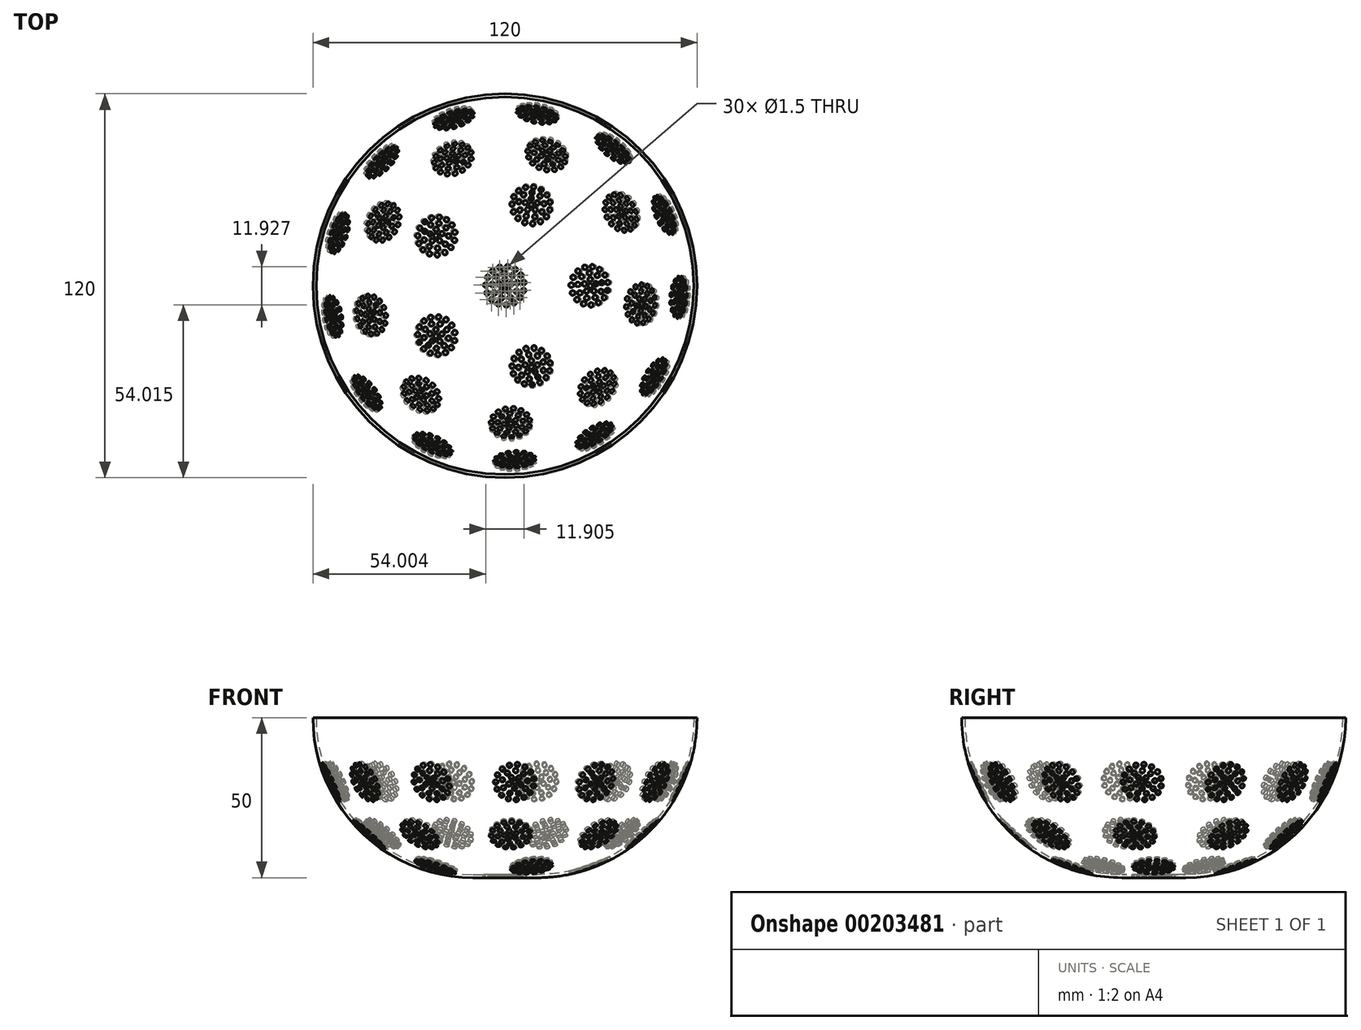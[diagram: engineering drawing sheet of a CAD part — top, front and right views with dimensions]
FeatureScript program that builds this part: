
annotation { "Feature Type Name" : "Feature", "Feature Type Description" : "" }
export const myFeature = defineFeature(function(context is Context, id is Id, definition is map)
    precondition{}
    {
        {
            var Q0;
            Q0=qCreatedBy(makeId("Front.planeOp"),FACE);
            var sketch = newSketch(context, id + "F0", { "sketchPlane" : qUnion([Q0])});
            skLineSegment(sketch, "E0", {"start": v(0, 0) * mm, "end": v(10, 0) * mm});
            skArc(sketch, "E1", {"start": v(10, 0) * mm, "mid": v(45.36, 14.64) * mm, "end": v(60, 50) * mm});
            skLineSegment(sketch, "E2", {"start": v(0, 0) * mm, "end": v(0, 50) * mm});
            skLineSegment(sketch, "E3", {"start": v(0, 50) * mm, "end": v(60, 50) * mm});
            skArc(sketch, "E4.0", {"start": v(10, 1) * mm, "mid": v(44.65, 15.35) * mm, "end": v(59, 50) * mm});
            skLineSegment(sketch, "E4.1", {"start": v(0, 1) * mm, "end": v(10, 1) * mm});
            skSolve(sketch);
        }
        {
            var Q0;
            {var subQ2=sQuery(id+"F0.wireOp",EDGE,"E0");Q0=makeQuery(id+"F0.imprint","IMPRINT",FACE,{"disambiguationData":[TD([[makeQuery(id+"F0.imprint","IMPRINT",EDGE,{"derivedFrom":subQ2}),1.0]])]});}
            var Q1;
            Q1=sQuery(id+"F0.wireOp",EDGE,"E2");
            revolve(context, id + "F1", {"entities" : qUnion([Q0]), "axis" : qUnion([Q1]), "revolveType" : RevolveType.FULL});
        }
        {
            var Q0;
            Q0=makeQuery(id+"F1.opRevolve","SWEPT_FACE",FACE,{"disambiguationData":[OSD([sQuery(id+"F0.wireOp",EDGE,"E4.1")])]});
            var sketch = newSketch(context, id + "F2", { "sketchPlane" : qUnion([Q0])});
            skCircle(sketch, "E5", {"center": v(0, 0) * mm, "radius": 0.75 * mm});
            skCircle(sketch, "E6", {"center": v(0, 2) * mm, "radius": 0.75 * mm});
            skCircle(sketch, "E7.1.0", {"center": v(-1.9, 0.62) * mm, "radius": 0.75 * mm});
            skCircle(sketch, "E7.2.0", {"center": v(-1.18, -1.62) * mm, "radius": 0.75 * mm});
            skCircle(sketch, "E7.3.0", {"center": v(1.18, -1.62) * mm, "radius": 0.75 * mm});
            skCircle(sketch, "E7.4.0", {"center": v(1.9, 0.62) * mm, "radius": 0.75 * mm});
            skLineSegment(sketch, "E8", {"start": v(0, 2) * mm, "end": v(1.9, 0.62) * mm, "construction": true});
            skLineSegment(sketch, "E9", {"start": v(0, 0) * mm, "end": v(0.95, 1.3) * mm, "construction": true});
            skLineSegment(sketch, "E10", {"start": v(0.95, 1.3) * mm, "end": v(2.35, 3.24) * mm, "construction": true});
            skCircle(sketch, "E11", {"center": v(2.35, 3.24) * mm, "radius": 0.75 * mm});
            skCircle(sketch, "E12.1.0", {"center": v(-0.28, 4) * mm, "radius": 0.75 * mm});
            skCircle(sketch, "E12.2.0", {"center": v(-2.78, 2.88) * mm, "radius": 0.75 * mm});
            skCircle(sketch, "E12.3.0", {"center": v(-3.98, 0.42) * mm, "radius": 0.75 * mm});
            skCircle(sketch, "E12.4.0", {"center": v(-3.32, -2.24) * mm, "radius": 0.75 * mm});
            skCircle(sketch, "E12.5.0", {"center": v(-1.1, -3.85) * mm, "radius": 0.75 * mm});
            skCircle(sketch, "E12.6.0", {"center": v(1.63, -3.65) * mm, "radius": 0.75 * mm});
            skCircle(sketch, "E13.1.7.0", {"center": v(3.6, -1.75) * mm, "radius": 0.75 * mm});
            skCircle(sketch, "E13.1.8.0", {"center": v(3.88, 0.97) * mm, "radius": 0.75 * mm});
            skLineSegment(sketch, "E14", {"start": v(3.88, 0.97) * mm, "end": v(2.35, 3.24) * mm, "construction": true});
            skLineSegment(sketch, "E15", {"start": v(0, 0) * mm, "end": v(3.12, 2.1) * mm, "construction": true});
            skLineSegment(sketch, "E16", {"start": v(3.12, 2.1) * mm, "end": v(4.97, 3.36) * mm, "construction": true});
            skCircle(sketch, "E17", {"center": v(4.97, 3.36) * mm, "radius": 0.75 * mm});
            skCircle(sketch, "E18.1.0", {"center": v(3.18, 5.09) * mm, "radius": 0.75 * mm});
            skCircle(sketch, "E18.2.0", {"center": v(0.84, 5.94) * mm, "radius": 0.75 * mm});
            skCircle(sketch, "E18.3.0", {"center": v(-1.65, 5.77) * mm, "radius": 0.75 * mm});
            skCircle(sketch, "E18.4.0", {"center": v(-3.86, 4.6) * mm, "radius": 0.75 * mm});
            skCircle(sketch, "E18.5.0", {"center": v(-5.4, 2.63) * mm, "radius": 0.75 * mm});
            skCircle(sketch, "E18.6.0", {"center": v(-6, 0.2) * mm, "radius": 0.75 * mm});
            skCircle(sketch, "E18.7.0", {"center": v(-5.56, -2.25) * mm, "radius": 0.75 * mm});
            skCircle(sketch, "E18.8.0", {"center": v(-4.17, -4.32) * mm, "radius": 0.75 * mm});
            skCircle(sketch, "E18.9.0", {"center": v(-2.05, -5.64) * mm, "radius": 0.75 * mm});
            skCircle(sketch, "E18.10.0", {"center": v(0.42, -5.99) * mm, "radius": 0.75 * mm});
            skCircle(sketch, "E18.11.0", {"center": v(2.82, -5.3) * mm, "radius": 0.75 * mm});
            skCircle(sketch, "E18.12.0", {"center": v(4.73, -3.7) * mm, "radius": 0.75 * mm});
            skCircle(sketch, "E18.13.0", {"center": v(5.82, -1.45) * mm, "radius": 0.75 * mm});
            skCircle(sketch, "E18.14.0", {"center": v(5.9, 1.04) * mm, "radius": 0.75 * mm});
            skSolve(sketch);
        }
        {
            var Q0;
            Q0=qSketchRegion(id+"F2",true);
            extrude(context, id + "F3", {"entities" : qUnion([Q0]), "operationType" : NewBodyOperationType.REMOVE, "oppositeDirection" : true, "depth" : 25 * mm});
        }
        {
            var Q0;
            Q0=makeQuery(id+"F1.opRevolve","SWEPT_FACE",FACE,{"disambiguationData":[OSD([sQuery(id+"F0.wireOp",EDGE,"E3")])]});
            var sketch = newSketch(context, id + "F4", { "sketchPlane" : qUnion([Q0])});
            skLineSegment(sketch, "E19", {"start": v(0, 59) * mm, "end": v(0, -59) * mm});
            skLineSegment(sketch, "E20", {"start": v(0, 0) * mm, "end": v(-31.56, 49.85) * mm});
            skLineSegment(sketch, "E21", {"start": v(0, 0) * mm, "end": v(-46.28, 36.6) * mm});
            skSolve(sketch);
        }
        {
            var Q0;
            Q0=makeQuery(id+"F3.boolean.opBoolean","COPY",FACE,{"derivedFrom":makeQuery(id+"F3.opExtrude","SWEPT_FACE",FACE,{"disambiguationData":[OSD([sQuery(id+"F2.wireOp",EDGE,"E18.7.0")])]})});
            var Q1;
            Q1=makeQuery(id+"F3.boolean.opBoolean","COPY",FACE,{"derivedFrom":makeQuery(id+"F3.opExtrude","SWEPT_FACE",FACE,{"disambiguationData":[OSD([sQuery(id+"F2.wireOp",EDGE,"E18.6.0")])]})});
            var Q2;
            Q2=makeQuery(id+"F3.boolean.opBoolean","COPY",FACE,{"derivedFrom":makeQuery(id+"F3.opExtrude","SWEPT_FACE",FACE,{"disambiguationData":[OSD([sQuery(id+"F2.wireOp",EDGE,"E18.5.0")])]})});
            var Q3;
            Q3=makeQuery(id+"F3.boolean.opBoolean","COPY",FACE,{"derivedFrom":makeQuery(id+"F3.opExtrude","SWEPT_FACE",FACE,{"disambiguationData":[OSD([sQuery(id+"F2.wireOp",EDGE,"E18.4.0")])]})});
            var Q4;
            Q4=makeQuery(id+"F3.boolean.opBoolean","COPY",FACE,{"derivedFrom":makeQuery(id+"F3.opExtrude","SWEPT_FACE",FACE,{"disambiguationData":[OSD([sQuery(id+"F2.wireOp",EDGE,"E18.3.0")])]})});
            var Q5;
            Q5=makeQuery(id+"F3.boolean.opBoolean","COPY",FACE,{"derivedFrom":makeQuery(id+"F3.opExtrude","SWEPT_FACE",FACE,{"disambiguationData":[OSD([sQuery(id+"F2.wireOp",EDGE,"E18.2.0")])]})});
            var Q6;
            Q6=makeQuery(id+"F3.boolean.opBoolean","COPY",FACE,{"derivedFrom":makeQuery(id+"F3.opExtrude","SWEPT_FACE",FACE,{"disambiguationData":[OSD([sQuery(id+"F2.wireOp",EDGE,"E18.1.0")])]})});
            var Q7;
            Q7=makeQuery(id+"F3.boolean.opBoolean","COPY",FACE,{"derivedFrom":makeQuery(id+"F3.opExtrude","SWEPT_FACE",FACE,{"disambiguationData":[OSD([sQuery(id+"F2.wireOp",EDGE,"E17")])]})});
            var Q8;
            Q8=makeQuery(id+"F3.boolean.opBoolean","COPY",FACE,{"derivedFrom":makeQuery(id+"F3.opExtrude","SWEPT_FACE",FACE,{"disambiguationData":[OSD([sQuery(id+"F2.wireOp",EDGE,"E18.14.0")])]})});
            var Q9;
            Q9=makeQuery(id+"F3.boolean.opBoolean","COPY",FACE,{"derivedFrom":makeQuery(id+"F3.opExtrude","SWEPT_FACE",FACE,{"disambiguationData":[OSD([sQuery(id+"F2.wireOp",EDGE,"E18.13.0")])]})});
            var Q10;
            Q10=makeQuery(id+"F3.boolean.opBoolean","COPY",FACE,{"derivedFrom":makeQuery(id+"F3.opExtrude","SWEPT_FACE",FACE,{"disambiguationData":[OSD([sQuery(id+"F2.wireOp",EDGE,"E18.12.0")])]})});
            var Q11;
            Q11=makeQuery(id+"F3.boolean.opBoolean","COPY",FACE,{"derivedFrom":makeQuery(id+"F3.opExtrude","SWEPT_FACE",FACE,{"disambiguationData":[OSD([sQuery(id+"F2.wireOp",EDGE,"E18.11.0")])]})});
            var Q12;
            Q12=makeQuery(id+"F3.boolean.opBoolean","COPY",FACE,{"derivedFrom":makeQuery(id+"F3.opExtrude","SWEPT_FACE",FACE,{"disambiguationData":[OSD([sQuery(id+"F2.wireOp",EDGE,"E18.10.0")])]})});
            var Q13;
            Q13=makeQuery(id+"F3.boolean.opBoolean","COPY",FACE,{"derivedFrom":makeQuery(id+"F3.opExtrude","SWEPT_FACE",FACE,{"disambiguationData":[OSD([sQuery(id+"F2.wireOp",EDGE,"E18.9.0")])]})});
            var Q14;
            Q14=makeQuery(id+"F3.boolean.opBoolean","COPY",FACE,{"derivedFrom":makeQuery(id+"F3.opExtrude","SWEPT_FACE",FACE,{"disambiguationData":[OSD([sQuery(id+"F2.wireOp",EDGE,"E18.8.0")])]})});
            var Q15;
            Q15=makeQuery(id+"F3.boolean.opBoolean","COPY",FACE,{"derivedFrom":makeQuery(id+"F3.opExtrude","SWEPT_FACE",FACE,{"disambiguationData":[OSD([sQuery(id+"F2.wireOp",EDGE,"E12.4.0")])]})});
            var Q16;
            Q16=makeQuery(id+"F3.boolean.opBoolean","COPY",FACE,{"derivedFrom":makeQuery(id+"F3.opExtrude","SWEPT_FACE",FACE,{"disambiguationData":[OSD([sQuery(id+"F2.wireOp",EDGE,"E12.3.0")])]})});
            var Q17;
            Q17=makeQuery(id+"F3.boolean.opBoolean","COPY",FACE,{"derivedFrom":makeQuery(id+"F3.opExtrude","SWEPT_FACE",FACE,{"disambiguationData":[OSD([sQuery(id+"F2.wireOp",EDGE,"E12.2.0")])]})});
            var Q18;
            Q18=makeQuery(id+"F3.boolean.opBoolean","COPY",FACE,{"derivedFrom":makeQuery(id+"F3.opExtrude","SWEPT_FACE",FACE,{"disambiguationData":[OSD([sQuery(id+"F2.wireOp",EDGE,"E12.1.0")])]})});
            var Q19;
            Q19=makeQuery(id+"F3.boolean.opBoolean","COPY",FACE,{"derivedFrom":makeQuery(id+"F3.opExtrude","SWEPT_FACE",FACE,{"disambiguationData":[OSD([sQuery(id+"F2.wireOp",EDGE,"E11")])]})});
            var Q20;
            Q20=makeQuery(id+"F3.boolean.opBoolean","COPY",FACE,{"derivedFrom":makeQuery(id+"F3.opExtrude","SWEPT_FACE",FACE,{"disambiguationData":[OSD([sQuery(id+"F2.wireOp",EDGE,"E13.1.8.0")])]})});
            var Q21;
            Q21=makeQuery(id+"F3.boolean.opBoolean","COPY",FACE,{"derivedFrom":makeQuery(id+"F3.opExtrude","SWEPT_FACE",FACE,{"disambiguationData":[OSD([sQuery(id+"F2.wireOp",EDGE,"E13.1.7.0")])]})});
            var Q22;
            Q22=makeQuery(id+"F3.boolean.opBoolean","COPY",FACE,{"derivedFrom":makeQuery(id+"F3.opExtrude","SWEPT_FACE",FACE,{"disambiguationData":[OSD([sQuery(id+"F2.wireOp",EDGE,"E12.6.0")])]})});
            var Q23;
            Q23=makeQuery(id+"F3.boolean.opBoolean","COPY",FACE,{"derivedFrom":makeQuery(id+"F3.opExtrude","SWEPT_FACE",FACE,{"disambiguationData":[OSD([sQuery(id+"F2.wireOp",EDGE,"E12.5.0")])]})});
            var Q24;
            Q24=makeQuery(id+"F3.boolean.opBoolean","COPY",FACE,{"derivedFrom":makeQuery(id+"F3.opExtrude","SWEPT_FACE",FACE,{"disambiguationData":[OSD([sQuery(id+"F2.wireOp",EDGE,"E7.2.0")])]})});
            var Q25;
            Q25=makeQuery(id+"F3.boolean.opBoolean","COPY",FACE,{"derivedFrom":makeQuery(id+"F3.opExtrude","SWEPT_FACE",FACE,{"disambiguationData":[OSD([sQuery(id+"F2.wireOp",EDGE,"E7.1.0")])]})});
            var Q26;
            Q26=makeQuery(id+"F3.boolean.opBoolean","COPY",FACE,{"derivedFrom":makeQuery(id+"F3.opExtrude","SWEPT_FACE",FACE,{"disambiguationData":[OSD([sQuery(id+"F2.wireOp",EDGE,"E6")])]})});
            var Q27;
            Q27=makeQuery(id+"F3.boolean.opBoolean","COPY",FACE,{"derivedFrom":makeQuery(id+"F3.opExtrude","SWEPT_FACE",FACE,{"disambiguationData":[OSD([sQuery(id+"F2.wireOp",EDGE,"E7.4.0")])]})});
            var Q28;
            Q28=makeQuery(id+"F3.boolean.opBoolean","COPY",FACE,{"derivedFrom":makeQuery(id+"F3.opExtrude","SWEPT_FACE",FACE,{"disambiguationData":[OSD([sQuery(id+"F2.wireOp",EDGE,"E7.3.0")])]})});
            var Q29;
            Q29=makeQuery(id+"F3.boolean.opBoolean","COPY",FACE,{"derivedFrom":makeQuery(id+"F3.opExtrude","SWEPT_FACE",FACE,{"disambiguationData":[OSD([sQuery(id+"F2.wireOp",EDGE,"E5")])]})});
            var Q30;
            Q30=sQuery(id+"F4.wireOp",EDGE,"E19");
            circularPattern(context, id + "F5", {"faces" : qUnion([Q0, Q1, Q2, Q3, Q4, Q5, Q6, Q7, Q8, Q9, Q10, Q11, Q12, Q13, Q14, Q15, Q16, Q17, Q18, Q19, Q20, Q21, Q22, Q23, Q24, Q25, Q26, Q27, Q28, Q29]), "axis" : qUnion([Q30]), "angle" : 30 * degree, "instanceCount" : 2, "patternType" : PatternType.FACE});
        }
        {
            var Q0;
            Q0=makeQuery(id+"F5.opPattern","COPY",FACE,{"derivedFrom":makeQuery(id+"F3.boolean.opBoolean","COPY",FACE,{"derivedFrom":makeQuery(id+"F3.opExtrude","SWEPT_FACE",FACE,{"disambiguationData":[OSD([sQuery(id+"F2.wireOp",EDGE,"E18.5.0")])]})}),"instanceName":"1"});
            var Q1;
            Q1=makeQuery(id+"F5.opPattern","COPY",FACE,{"derivedFrom":makeQuery(id+"F3.boolean.opBoolean","COPY",FACE,{"derivedFrom":makeQuery(id+"F3.opExtrude","SWEPT_FACE",FACE,{"disambiguationData":[OSD([sQuery(id+"F2.wireOp",EDGE,"E18.6.0")])]})}),"instanceName":"1"});
            var Q2;
            Q2=makeQuery(id+"F5.opPattern","COPY",FACE,{"derivedFrom":makeQuery(id+"F3.boolean.opBoolean","COPY",FACE,{"derivedFrom":makeQuery(id+"F3.opExtrude","SWEPT_FACE",FACE,{"disambiguationData":[OSD([sQuery(id+"F2.wireOp",EDGE,"E18.7.0")])]})}),"instanceName":"1"});
            var Q3;
            Q3=makeQuery(id+"F5.opPattern","COPY",FACE,{"derivedFrom":makeQuery(id+"F3.boolean.opBoolean","COPY",FACE,{"derivedFrom":makeQuery(id+"F3.opExtrude","SWEPT_FACE",FACE,{"disambiguationData":[OSD([sQuery(id+"F2.wireOp",EDGE,"E18.8.0")])]})}),"instanceName":"1"});
            var Q4;
            Q4=makeQuery(id+"F5.opPattern","COPY",FACE,{"derivedFrom":makeQuery(id+"F3.boolean.opBoolean","COPY",FACE,{"derivedFrom":makeQuery(id+"F3.opExtrude","SWEPT_FACE",FACE,{"disambiguationData":[OSD([sQuery(id+"F2.wireOp",EDGE,"E18.9.0")])]})}),"instanceName":"1"});
            var Q5;
            Q5=makeQuery(id+"F5.opPattern","COPY",FACE,{"derivedFrom":makeQuery(id+"F3.boolean.opBoolean","COPY",FACE,{"derivedFrom":makeQuery(id+"F3.opExtrude","SWEPT_FACE",FACE,{"disambiguationData":[OSD([sQuery(id+"F2.wireOp",EDGE,"E18.11.0")])]})}),"instanceName":"1"});
            var Q6;
            Q6=makeQuery(id+"F5.opPattern","COPY",FACE,{"derivedFrom":makeQuery(id+"F3.boolean.opBoolean","COPY",FACE,{"derivedFrom":makeQuery(id+"F3.opExtrude","SWEPT_FACE",FACE,{"disambiguationData":[OSD([sQuery(id+"F2.wireOp",EDGE,"E18.12.0")])]})}),"instanceName":"1"});
            var Q7;
            Q7=makeQuery(id+"F5.opPattern","COPY",FACE,{"derivedFrom":makeQuery(id+"F3.boolean.opBoolean","COPY",FACE,{"derivedFrom":makeQuery(id+"F3.opExtrude","SWEPT_FACE",FACE,{"disambiguationData":[OSD([sQuery(id+"F2.wireOp",EDGE,"E18.13.0")])]})}),"instanceName":"1"});
            var Q8;
            Q8=makeQuery(id+"F5.opPattern","COPY",FACE,{"derivedFrom":makeQuery(id+"F3.boolean.opBoolean","COPY",FACE,{"derivedFrom":makeQuery(id+"F3.opExtrude","SWEPT_FACE",FACE,{"disambiguationData":[OSD([sQuery(id+"F2.wireOp",EDGE,"E18.14.0")])]})}),"instanceName":"1"});
            var Q9;
            Q9=makeQuery(id+"F5.opPattern","COPY",FACE,{"derivedFrom":makeQuery(id+"F3.boolean.opBoolean","COPY",FACE,{"derivedFrom":makeQuery(id+"F3.opExtrude","SWEPT_FACE",FACE,{"disambiguationData":[OSD([sQuery(id+"F2.wireOp",EDGE,"E17")])]})}),"instanceName":"1"});
            var Q10;
            Q10=makeQuery(id+"F5.opPattern","COPY",FACE,{"derivedFrom":makeQuery(id+"F3.boolean.opBoolean","COPY",FACE,{"derivedFrom":makeQuery(id+"F3.opExtrude","SWEPT_FACE",FACE,{"disambiguationData":[OSD([sQuery(id+"F2.wireOp",EDGE,"E18.1.0")])]})}),"instanceName":"1"});
            var Q11;
            Q11=makeQuery(id+"F5.opPattern","COPY",FACE,{"derivedFrom":makeQuery(id+"F3.boolean.opBoolean","COPY",FACE,{"derivedFrom":makeQuery(id+"F3.opExtrude","SWEPT_FACE",FACE,{"disambiguationData":[OSD([sQuery(id+"F2.wireOp",EDGE,"E18.2.0")])]})}),"instanceName":"1"});
            var Q12;
            Q12=makeQuery(id+"F5.opPattern","COPY",FACE,{"derivedFrom":makeQuery(id+"F3.boolean.opBoolean","COPY",FACE,{"derivedFrom":makeQuery(id+"F3.opExtrude","SWEPT_FACE",FACE,{"disambiguationData":[OSD([sQuery(id+"F2.wireOp",EDGE,"E18.3.0")])]})}),"instanceName":"1"});
            var Q13;
            Q13=makeQuery(id+"F5.opPattern","COPY",FACE,{"derivedFrom":makeQuery(id+"F3.boolean.opBoolean","COPY",FACE,{"derivedFrom":makeQuery(id+"F3.opExtrude","SWEPT_FACE",FACE,{"disambiguationData":[OSD([sQuery(id+"F2.wireOp",EDGE,"E18.4.0")])]})}),"instanceName":"1"});
            var Q14;
            Q14=makeQuery(id+"F5.opPattern","COPY",FACE,{"derivedFrom":makeQuery(id+"F3.boolean.opBoolean","COPY",FACE,{"derivedFrom":makeQuery(id+"F3.opExtrude","SWEPT_FACE",FACE,{"disambiguationData":[OSD([sQuery(id+"F2.wireOp",EDGE,"E12.2.0")])]})}),"instanceName":"1"});
            var Q15;
            Q15=makeQuery(id+"F5.opPattern","COPY",FACE,{"derivedFrom":makeQuery(id+"F3.boolean.opBoolean","COPY",FACE,{"derivedFrom":makeQuery(id+"F3.opExtrude","SWEPT_FACE",FACE,{"disambiguationData":[OSD([sQuery(id+"F2.wireOp",EDGE,"E12.3.0")])]})}),"instanceName":"1"});
            var Q16;
            Q16=makeQuery(id+"F5.opPattern","COPY",FACE,{"derivedFrom":makeQuery(id+"F3.boolean.opBoolean","COPY",FACE,{"derivedFrom":makeQuery(id+"F3.opExtrude","SWEPT_FACE",FACE,{"disambiguationData":[OSD([sQuery(id+"F2.wireOp",EDGE,"E12.4.0")])]})}),"instanceName":"1"});
            var Q17;
            Q17=makeQuery(id+"F5.opPattern","COPY",FACE,{"derivedFrom":makeQuery(id+"F3.boolean.opBoolean","COPY",FACE,{"derivedFrom":makeQuery(id+"F3.opExtrude","SWEPT_FACE",FACE,{"disambiguationData":[OSD([sQuery(id+"F2.wireOp",EDGE,"E12.6.0")])]})}),"instanceName":"1"});
            var Q18;
            Q18=makeQuery(id+"F5.opPattern","COPY",FACE,{"derivedFrom":makeQuery(id+"F3.boolean.opBoolean","COPY",FACE,{"derivedFrom":makeQuery(id+"F3.opExtrude","SWEPT_FACE",FACE,{"disambiguationData":[OSD([sQuery(id+"F2.wireOp",EDGE,"E13.1.7.0")])]})}),"instanceName":"1"});
            var Q19;
            Q19=makeQuery(id+"F5.opPattern","COPY",FACE,{"derivedFrom":makeQuery(id+"F3.boolean.opBoolean","COPY",FACE,{"derivedFrom":makeQuery(id+"F3.opExtrude","SWEPT_FACE",FACE,{"disambiguationData":[OSD([sQuery(id+"F2.wireOp",EDGE,"E18.10.0")])]})}),"instanceName":"1"});
            var Q20;
            Q20=makeQuery(id+"F5.opPattern","COPY",FACE,{"derivedFrom":makeQuery(id+"F3.boolean.opBoolean","COPY",FACE,{"derivedFrom":makeQuery(id+"F3.opExtrude","SWEPT_FACE",FACE,{"disambiguationData":[OSD([sQuery(id+"F2.wireOp",EDGE,"E12.5.0")])]})}),"instanceName":"1"});
            var Q21;
            Q21=makeQuery(id+"F5.opPattern","COPY",FACE,{"derivedFrom":makeQuery(id+"F3.boolean.opBoolean","COPY",FACE,{"derivedFrom":makeQuery(id+"F3.opExtrude","SWEPT_FACE",FACE,{"disambiguationData":[OSD([sQuery(id+"F2.wireOp",EDGE,"E7.2.0")])]})}),"instanceName":"1"});
            var Q22;
            Q22=makeQuery(id+"F5.opPattern","COPY",FACE,{"derivedFrom":makeQuery(id+"F3.boolean.opBoolean","COPY",FACE,{"derivedFrom":makeQuery(id+"F3.opExtrude","SWEPT_FACE",FACE,{"disambiguationData":[OSD([sQuery(id+"F2.wireOp",EDGE,"E5")])]})}),"instanceName":"1"});
            var Q23;
            Q23=makeQuery(id+"F5.opPattern","COPY",FACE,{"derivedFrom":makeQuery(id+"F3.boolean.opBoolean","COPY",FACE,{"derivedFrom":makeQuery(id+"F3.opExtrude","SWEPT_FACE",FACE,{"disambiguationData":[OSD([sQuery(id+"F2.wireOp",EDGE,"E6")])]})}),"instanceName":"1"});
            var Q24;
            Q24=makeQuery(id+"F5.opPattern","COPY",FACE,{"derivedFrom":makeQuery(id+"F3.boolean.opBoolean","COPY",FACE,{"derivedFrom":makeQuery(id+"F3.opExtrude","SWEPT_FACE",FACE,{"disambiguationData":[OSD([sQuery(id+"F2.wireOp",EDGE,"E7.4.0")])]})}),"instanceName":"1"});
            var Q25;
            Q25=makeQuery(id+"F5.opPattern","COPY",FACE,{"derivedFrom":makeQuery(id+"F3.boolean.opBoolean","COPY",FACE,{"derivedFrom":makeQuery(id+"F3.opExtrude","SWEPT_FACE",FACE,{"disambiguationData":[OSD([sQuery(id+"F2.wireOp",EDGE,"E7.3.0")])]})}),"instanceName":"1"});
            var Q26;
            Q26=makeQuery(id+"F5.opPattern","COPY",FACE,{"derivedFrom":makeQuery(id+"F3.boolean.opBoolean","COPY",FACE,{"derivedFrom":makeQuery(id+"F3.opExtrude","SWEPT_FACE",FACE,{"disambiguationData":[OSD([sQuery(id+"F2.wireOp",EDGE,"E13.1.8.0")])]})}),"instanceName":"1"});
            var Q27;
            Q27=makeQuery(id+"F5.opPattern","COPY",FACE,{"derivedFrom":makeQuery(id+"F3.boolean.opBoolean","COPY",FACE,{"derivedFrom":makeQuery(id+"F3.opExtrude","SWEPT_FACE",FACE,{"disambiguationData":[OSD([sQuery(id+"F2.wireOp",EDGE,"E11")])]})}),"instanceName":"1"});
            var Q28;
            Q28=makeQuery(id+"F5.opPattern","COPY",FACE,{"derivedFrom":makeQuery(id+"F3.boolean.opBoolean","COPY",FACE,{"derivedFrom":makeQuery(id+"F3.opExtrude","SWEPT_FACE",FACE,{"disambiguationData":[OSD([sQuery(id+"F2.wireOp",EDGE,"E12.1.0")])]})}),"instanceName":"1"});
            var Q29;
            Q29=makeQuery(id+"F5.opPattern","COPY",FACE,{"derivedFrom":makeQuery(id+"F3.boolean.opBoolean","COPY",FACE,{"derivedFrom":makeQuery(id+"F3.opExtrude","SWEPT_FACE",FACE,{"disambiguationData":[OSD([sQuery(id+"F2.wireOp",EDGE,"E7.1.0")])]})}),"instanceName":"1"});
            var Q30;
            Q30=sQuery(id+"F0.wireOp",EDGE,"E2");
            circularPattern(context, id + "F6", {"faces" : qUnion([Q0, Q1, Q2, Q3, Q4, Q5, Q6, Q7, Q8, Q9, Q10, Q11, Q12, Q13, Q14, Q15, Q16, Q17, Q18, Q19, Q20, Q21, Q22, Q23, Q24, Q25, Q26, Q27, Q28, Q29]), "axis" : qUnion([Q30]), "angle" : 360 * degree, "instanceCount" : 5, "equalSpace" : true, "patternType" : PatternType.FACE});
        }
        {
            var Q0;
            Q0=makeQuery(id+"F3.boolean.opBoolean","COPY",FACE,{"derivedFrom":makeQuery(id+"F3.opExtrude","SWEPT_FACE",FACE,{"disambiguationData":[OSD([sQuery(id+"F2.wireOp",EDGE,"E18.1.0")])]})});
            var Q1;
            Q1=makeQuery(id+"F3.boolean.opBoolean","COPY",FACE,{"derivedFrom":makeQuery(id+"F3.opExtrude","SWEPT_FACE",FACE,{"disambiguationData":[OSD([sQuery(id+"F2.wireOp",EDGE,"E18.2.0")])]})});
            var Q2;
            Q2=makeQuery(id+"F3.boolean.opBoolean","COPY",FACE,{"derivedFrom":makeQuery(id+"F3.opExtrude","SWEPT_FACE",FACE,{"disambiguationData":[OSD([sQuery(id+"F2.wireOp",EDGE,"E18.3.0")])]})});
            var Q3;
            Q3=makeQuery(id+"F3.boolean.opBoolean","COPY",FACE,{"derivedFrom":makeQuery(id+"F3.opExtrude","SWEPT_FACE",FACE,{"disambiguationData":[OSD([sQuery(id+"F2.wireOp",EDGE,"E18.4.0")])]})});
            var Q4;
            Q4=makeQuery(id+"F3.boolean.opBoolean","COPY",FACE,{"derivedFrom":makeQuery(id+"F3.opExtrude","SWEPT_FACE",FACE,{"disambiguationData":[OSD([sQuery(id+"F2.wireOp",EDGE,"E18.5.0")])]})});
            var Q5;
            Q5=makeQuery(id+"F3.boolean.opBoolean","COPY",FACE,{"derivedFrom":makeQuery(id+"F3.opExtrude","SWEPT_FACE",FACE,{"disambiguationData":[OSD([sQuery(id+"F2.wireOp",EDGE,"E18.6.0")])]})});
            var Q6;
            Q6=makeQuery(id+"F3.boolean.opBoolean","COPY",FACE,{"derivedFrom":makeQuery(id+"F3.opExtrude","SWEPT_FACE",FACE,{"disambiguationData":[OSD([sQuery(id+"F2.wireOp",EDGE,"E18.7.0")])]})});
            var Q7;
            Q7=makeQuery(id+"F3.boolean.opBoolean","COPY",FACE,{"derivedFrom":makeQuery(id+"F3.opExtrude","SWEPT_FACE",FACE,{"disambiguationData":[OSD([sQuery(id+"F2.wireOp",EDGE,"E18.8.0")])]})});
            var Q8;
            Q8=makeQuery(id+"F3.boolean.opBoolean","COPY",FACE,{"derivedFrom":makeQuery(id+"F3.opExtrude","SWEPT_FACE",FACE,{"disambiguationData":[OSD([sQuery(id+"F2.wireOp",EDGE,"E18.9.0")])]})});
            var Q9;
            Q9=makeQuery(id+"F3.boolean.opBoolean","COPY",FACE,{"derivedFrom":makeQuery(id+"F3.opExtrude","SWEPT_FACE",FACE,{"disambiguationData":[OSD([sQuery(id+"F2.wireOp",EDGE,"E18.10.0")])]})});
            var Q10;
            Q10=makeQuery(id+"F3.boolean.opBoolean","COPY",FACE,{"derivedFrom":makeQuery(id+"F3.opExtrude","SWEPT_FACE",FACE,{"disambiguationData":[OSD([sQuery(id+"F2.wireOp",EDGE,"E18.11.0")])]})});
            var Q11;
            Q11=makeQuery(id+"F3.boolean.opBoolean","COPY",FACE,{"derivedFrom":makeQuery(id+"F3.opExtrude","SWEPT_FACE",FACE,{"disambiguationData":[OSD([sQuery(id+"F2.wireOp",EDGE,"E18.12.0")])]})});
            var Q12;
            Q12=makeQuery(id+"F3.boolean.opBoolean","COPY",FACE,{"derivedFrom":makeQuery(id+"F3.opExtrude","SWEPT_FACE",FACE,{"disambiguationData":[OSD([sQuery(id+"F2.wireOp",EDGE,"E18.13.0")])]})});
            var Q13;
            Q13=makeQuery(id+"F3.boolean.opBoolean","COPY",FACE,{"derivedFrom":makeQuery(id+"F3.opExtrude","SWEPT_FACE",FACE,{"disambiguationData":[OSD([sQuery(id+"F2.wireOp",EDGE,"E18.14.0")])]})});
            var Q14;
            Q14=makeQuery(id+"F3.boolean.opBoolean","COPY",FACE,{"derivedFrom":makeQuery(id+"F3.opExtrude","SWEPT_FACE",FACE,{"disambiguationData":[OSD([sQuery(id+"F2.wireOp",EDGE,"E13.1.8.0")])]})});
            var Q15;
            Q15=makeQuery(id+"F3.boolean.opBoolean","COPY",FACE,{"derivedFrom":makeQuery(id+"F3.opExtrude","SWEPT_FACE",FACE,{"disambiguationData":[OSD([sQuery(id+"F2.wireOp",EDGE,"E11")])]})});
            var Q16;
            Q16=makeQuery(id+"F3.boolean.opBoolean","COPY",FACE,{"derivedFrom":makeQuery(id+"F3.opExtrude","SWEPT_FACE",FACE,{"disambiguationData":[OSD([sQuery(id+"F2.wireOp",EDGE,"E12.1.0")])]})});
            var Q17;
            Q17=makeQuery(id+"F3.boolean.opBoolean","COPY",FACE,{"derivedFrom":makeQuery(id+"F3.opExtrude","SWEPT_FACE",FACE,{"disambiguationData":[OSD([sQuery(id+"F2.wireOp",EDGE,"E12.2.0")])]})});
            var Q18;
            Q18=makeQuery(id+"F3.boolean.opBoolean","COPY",FACE,{"derivedFrom":makeQuery(id+"F3.opExtrude","SWEPT_FACE",FACE,{"disambiguationData":[OSD([sQuery(id+"F2.wireOp",EDGE,"E12.3.0")])]})});
            var Q19;
            Q19=makeQuery(id+"F3.boolean.opBoolean","COPY",FACE,{"derivedFrom":makeQuery(id+"F3.opExtrude","SWEPT_FACE",FACE,{"disambiguationData":[OSD([sQuery(id+"F2.wireOp",EDGE,"E12.4.0")])]})});
            var Q20;
            Q20=makeQuery(id+"F3.boolean.opBoolean","COPY",FACE,{"derivedFrom":makeQuery(id+"F3.opExtrude","SWEPT_FACE",FACE,{"disambiguationData":[OSD([sQuery(id+"F2.wireOp",EDGE,"E12.5.0")])]})});
            var Q21;
            Q21=makeQuery(id+"F3.boolean.opBoolean","COPY",FACE,{"derivedFrom":makeQuery(id+"F3.opExtrude","SWEPT_FACE",FACE,{"disambiguationData":[OSD([sQuery(id+"F2.wireOp",EDGE,"E12.6.0")])]})});
            var Q22;
            Q22=makeQuery(id+"F3.boolean.opBoolean","COPY",FACE,{"derivedFrom":makeQuery(id+"F3.opExtrude","SWEPT_FACE",FACE,{"disambiguationData":[OSD([sQuery(id+"F2.wireOp",EDGE,"E13.1.7.0")])]})});
            var Q23;
            Q23=makeQuery(id+"F3.boolean.opBoolean","COPY",FACE,{"derivedFrom":makeQuery(id+"F3.opExtrude","SWEPT_FACE",FACE,{"disambiguationData":[OSD([sQuery(id+"F2.wireOp",EDGE,"E7.4.0")])]})});
            var Q24;
            Q24=makeQuery(id+"F3.boolean.opBoolean","COPY",FACE,{"derivedFrom":makeQuery(id+"F3.opExtrude","SWEPT_FACE",FACE,{"disambiguationData":[OSD([sQuery(id+"F2.wireOp",EDGE,"E6")])]})});
            var Q25;
            Q25=makeQuery(id+"F3.boolean.opBoolean","COPY",FACE,{"derivedFrom":makeQuery(id+"F3.opExtrude","SWEPT_FACE",FACE,{"disambiguationData":[OSD([sQuery(id+"F2.wireOp",EDGE,"E7.1.0")])]})});
            var Q26;
            Q26=makeQuery(id+"F3.boolean.opBoolean","COPY",FACE,{"derivedFrom":makeQuery(id+"F3.opExtrude","SWEPT_FACE",FACE,{"disambiguationData":[OSD([sQuery(id+"F2.wireOp",EDGE,"E7.2.0")])]})});
            var Q27;
            Q27=makeQuery(id+"F3.boolean.opBoolean","COPY",FACE,{"derivedFrom":makeQuery(id+"F3.opExtrude","SWEPT_FACE",FACE,{"disambiguationData":[OSD([sQuery(id+"F2.wireOp",EDGE,"E5")])]})});
            var Q28;
            Q28=makeQuery(id+"F3.boolean.opBoolean","COPY",FACE,{"derivedFrom":makeQuery(id+"F3.opExtrude","SWEPT_FACE",FACE,{"disambiguationData":[OSD([sQuery(id+"F2.wireOp",EDGE,"E7.3.0")])]})});
            var Q29;
            Q29=makeQuery(id+"F3.boolean.opBoolean","COPY",FACE,{"derivedFrom":makeQuery(id+"F3.opExtrude","SWEPT_FACE",FACE,{"disambiguationData":[OSD([sQuery(id+"F2.wireOp",EDGE,"E17")])]})});
            var Q30;
            Q30=sQuery(id+"F4.wireOp",EDGE,"E20");
            circularPattern(context, id + "F7", {"faces" : qUnion([Q0, Q1, Q2, Q3, Q4, Q5, Q6, Q7, Q8, Q9, Q10, Q11, Q12, Q13, Q14, Q15, Q16, Q17, Q18, Q19, Q20, Q21, Q22, Q23, Q24, Q25, Q26, Q27, Q28, Q29]), "axis" : qUnion([Q30]), "angle" : 50 * degree, "instanceCount" : 2, "oppositeDirection" : true, "patternType" : PatternType.FACE});
        }
        {
            var Q0;
            Q0=makeQuery(id+"F7.opPattern","COPY",FACE,{"derivedFrom":makeQuery(id+"F3.boolean.opBoolean","COPY",FACE,{"derivedFrom":makeQuery(id+"F3.opExtrude","SWEPT_FACE",FACE,{"disambiguationData":[OSD([sQuery(id+"F2.wireOp",EDGE,"E18.10.0")])]})}),"instanceName":"1"});
            var Q1;
            Q1=makeQuery(id+"F7.opPattern","COPY",FACE,{"derivedFrom":makeQuery(id+"F3.boolean.opBoolean","COPY",FACE,{"derivedFrom":makeQuery(id+"F3.opExtrude","SWEPT_FACE",FACE,{"disambiguationData":[OSD([sQuery(id+"F2.wireOp",EDGE,"E18.9.0")])]})}),"instanceName":"1"});
            var Q2;
            Q2=makeQuery(id+"F7.opPattern","COPY",FACE,{"derivedFrom":makeQuery(id+"F3.boolean.opBoolean","COPY",FACE,{"derivedFrom":makeQuery(id+"F3.opExtrude","SWEPT_FACE",FACE,{"disambiguationData":[OSD([sQuery(id+"F2.wireOp",EDGE,"E18.8.0")])]})}),"instanceName":"1"});
            var Q3;
            Q3=makeQuery(id+"F7.opPattern","COPY",FACE,{"derivedFrom":makeQuery(id+"F3.boolean.opBoolean","COPY",FACE,{"derivedFrom":makeQuery(id+"F3.opExtrude","SWEPT_FACE",FACE,{"disambiguationData":[OSD([sQuery(id+"F2.wireOp",EDGE,"E18.7.0")])]})}),"instanceName":"1"});
            var Q4;
            Q4=makeQuery(id+"F7.opPattern","COPY",FACE,{"derivedFrom":makeQuery(id+"F3.boolean.opBoolean","COPY",FACE,{"derivedFrom":makeQuery(id+"F3.opExtrude","SWEPT_FACE",FACE,{"disambiguationData":[OSD([sQuery(id+"F2.wireOp",EDGE,"E18.6.0")])]})}),"instanceName":"1"});
            var Q5;
            Q5=makeQuery(id+"F7.opPattern","COPY",FACE,{"derivedFrom":makeQuery(id+"F3.boolean.opBoolean","COPY",FACE,{"derivedFrom":makeQuery(id+"F3.opExtrude","SWEPT_FACE",FACE,{"disambiguationData":[OSD([sQuery(id+"F2.wireOp",EDGE,"E18.5.0")])]})}),"instanceName":"1"});
            var Q6;
            Q6=makeQuery(id+"F7.opPattern","COPY",FACE,{"derivedFrom":makeQuery(id+"F3.boolean.opBoolean","COPY",FACE,{"derivedFrom":makeQuery(id+"F3.opExtrude","SWEPT_FACE",FACE,{"disambiguationData":[OSD([sQuery(id+"F2.wireOp",EDGE,"E18.4.0")])]})}),"instanceName":"1"});
            var Q7;
            Q7=makeQuery(id+"F7.opPattern","COPY",FACE,{"derivedFrom":makeQuery(id+"F3.boolean.opBoolean","COPY",FACE,{"derivedFrom":makeQuery(id+"F3.opExtrude","SWEPT_FACE",FACE,{"disambiguationData":[OSD([sQuery(id+"F2.wireOp",EDGE,"E18.3.0")])]})}),"instanceName":"1"});
            var Q8;
            Q8=makeQuery(id+"F7.opPattern","COPY",FACE,{"derivedFrom":makeQuery(id+"F3.boolean.opBoolean","COPY",FACE,{"derivedFrom":makeQuery(id+"F3.opExtrude","SWEPT_FACE",FACE,{"disambiguationData":[OSD([sQuery(id+"F2.wireOp",EDGE,"E12.2.0")])]})}),"instanceName":"1"});
            var Q9;
            Q9=makeQuery(id+"F7.opPattern","COPY",FACE,{"derivedFrom":makeQuery(id+"F3.boolean.opBoolean","COPY",FACE,{"derivedFrom":makeQuery(id+"F3.opExtrude","SWEPT_FACE",FACE,{"disambiguationData":[OSD([sQuery(id+"F2.wireOp",EDGE,"E12.3.0")])]})}),"instanceName":"1"});
            var Q10;
            Q10=makeQuery(id+"F7.opPattern","COPY",FACE,{"derivedFrom":makeQuery(id+"F3.boolean.opBoolean","COPY",FACE,{"derivedFrom":makeQuery(id+"F3.opExtrude","SWEPT_FACE",FACE,{"disambiguationData":[OSD([sQuery(id+"F2.wireOp",EDGE,"E12.4.0")])]})}),"instanceName":"1"});
            var Q11;
            Q11=makeQuery(id+"F7.opPattern","COPY",FACE,{"derivedFrom":makeQuery(id+"F3.boolean.opBoolean","COPY",FACE,{"derivedFrom":makeQuery(id+"F3.opExtrude","SWEPT_FACE",FACE,{"disambiguationData":[OSD([sQuery(id+"F2.wireOp",EDGE,"E12.5.0")])]})}),"instanceName":"1"});
            var Q12;
            Q12=makeQuery(id+"F7.opPattern","COPY",FACE,{"derivedFrom":makeQuery(id+"F3.boolean.opBoolean","COPY",FACE,{"derivedFrom":makeQuery(id+"F3.opExtrude","SWEPT_FACE",FACE,{"disambiguationData":[OSD([sQuery(id+"F2.wireOp",EDGE,"E12.6.0")])]})}),"instanceName":"1"});
            var Q13;
            Q13=makeQuery(id+"F7.opPattern","COPY",FACE,{"derivedFrom":makeQuery(id+"F3.boolean.opBoolean","COPY",FACE,{"derivedFrom":makeQuery(id+"F3.opExtrude","SWEPT_FACE",FACE,{"disambiguationData":[OSD([sQuery(id+"F2.wireOp",EDGE,"E7.2.0")])]})}),"instanceName":"1"});
            var Q14;
            Q14=makeQuery(id+"F7.opPattern","COPY",FACE,{"derivedFrom":makeQuery(id+"F3.boolean.opBoolean","COPY",FACE,{"derivedFrom":makeQuery(id+"F3.opExtrude","SWEPT_FACE",FACE,{"disambiguationData":[OSD([sQuery(id+"F2.wireOp",EDGE,"E7.1.0")])]})}),"instanceName":"1"});
            var Q15;
            Q15=makeQuery(id+"F7.opPattern","COPY",FACE,{"derivedFrom":makeQuery(id+"F3.boolean.opBoolean","COPY",FACE,{"derivedFrom":makeQuery(id+"F3.opExtrude","SWEPT_FACE",FACE,{"disambiguationData":[OSD([sQuery(id+"F2.wireOp",EDGE,"E6")])]})}),"instanceName":"1"});
            var Q16;
            Q16=makeQuery(id+"F7.opPattern","COPY",FACE,{"derivedFrom":makeQuery(id+"F3.boolean.opBoolean","COPY",FACE,{"derivedFrom":makeQuery(id+"F3.opExtrude","SWEPT_FACE",FACE,{"disambiguationData":[OSD([sQuery(id+"F2.wireOp",EDGE,"E12.1.0")])]})}),"instanceName":"1"});
            var Q17;
            Q17=makeQuery(id+"F7.opPattern","COPY",FACE,{"derivedFrom":makeQuery(id+"F3.boolean.opBoolean","COPY",FACE,{"derivedFrom":makeQuery(id+"F3.opExtrude","SWEPT_FACE",FACE,{"disambiguationData":[OSD([sQuery(id+"F2.wireOp",EDGE,"E18.2.0")])]})}),"instanceName":"1"});
            var Q18;
            Q18=makeQuery(id+"F7.opPattern","COPY",FACE,{"derivedFrom":makeQuery(id+"F3.boolean.opBoolean","COPY",FACE,{"derivedFrom":makeQuery(id+"F3.opExtrude","SWEPT_FACE",FACE,{"disambiguationData":[OSD([sQuery(id+"F2.wireOp",EDGE,"E18.1.0")])]})}),"instanceName":"1"});
            var Q19;
            Q19=makeQuery(id+"F7.opPattern","COPY",FACE,{"derivedFrom":makeQuery(id+"F3.boolean.opBoolean","COPY",FACE,{"derivedFrom":makeQuery(id+"F3.opExtrude","SWEPT_FACE",FACE,{"disambiguationData":[OSD([sQuery(id+"F2.wireOp",EDGE,"E11")])]})}),"instanceName":"1"});
            var Q20;
            Q20=makeQuery(id+"F7.opPattern","COPY",FACE,{"derivedFrom":makeQuery(id+"F3.boolean.opBoolean","COPY",FACE,{"derivedFrom":makeQuery(id+"F3.opExtrude","SWEPT_FACE",FACE,{"disambiguationData":[OSD([sQuery(id+"F2.wireOp",EDGE,"E7.4.0")])]})}),"instanceName":"1"});
            var Q21;
            Q21=makeQuery(id+"F7.opPattern","COPY",FACE,{"derivedFrom":makeQuery(id+"F3.boolean.opBoolean","COPY",FACE,{"derivedFrom":makeQuery(id+"F3.opExtrude","SWEPT_FACE",FACE,{"disambiguationData":[OSD([sQuery(id+"F2.wireOp",EDGE,"E5")])]})}),"instanceName":"1"});
            var Q22;
            Q22=makeQuery(id+"F7.opPattern","COPY",FACE,{"derivedFrom":makeQuery(id+"F3.boolean.opBoolean","COPY",FACE,{"derivedFrom":makeQuery(id+"F3.opExtrude","SWEPT_FACE",FACE,{"disambiguationData":[OSD([sQuery(id+"F2.wireOp",EDGE,"E7.3.0")])]})}),"instanceName":"1"});
            var Q23;
            Q23=makeQuery(id+"F7.opPattern","COPY",FACE,{"derivedFrom":makeQuery(id+"F3.boolean.opBoolean","COPY",FACE,{"derivedFrom":makeQuery(id+"F3.opExtrude","SWEPT_FACE",FACE,{"disambiguationData":[OSD([sQuery(id+"F2.wireOp",EDGE,"E18.11.0")])]})}),"instanceName":"1"});
            var Q24;
            Q24=makeQuery(id+"F7.opPattern","COPY",FACE,{"derivedFrom":makeQuery(id+"F3.boolean.opBoolean","COPY",FACE,{"derivedFrom":makeQuery(id+"F3.opExtrude","SWEPT_FACE",FACE,{"disambiguationData":[OSD([sQuery(id+"F2.wireOp",EDGE,"E18.12.0")])]})}),"instanceName":"1"});
            var Q25;
            Q25=makeQuery(id+"F7.opPattern","COPY",FACE,{"derivedFrom":makeQuery(id+"F3.boolean.opBoolean","COPY",FACE,{"derivedFrom":makeQuery(id+"F3.opExtrude","SWEPT_FACE",FACE,{"disambiguationData":[OSD([sQuery(id+"F2.wireOp",EDGE,"E13.1.7.0")])]})}),"instanceName":"1"});
            var Q26;
            Q26=makeQuery(id+"F7.opPattern","COPY",FACE,{"derivedFrom":makeQuery(id+"F3.boolean.opBoolean","COPY",FACE,{"derivedFrom":makeQuery(id+"F3.opExtrude","SWEPT_FACE",FACE,{"disambiguationData":[OSD([sQuery(id+"F2.wireOp",EDGE,"E18.13.0")])]})}),"instanceName":"1"});
            var Q27;
            Q27=makeQuery(id+"F7.opPattern","COPY",FACE,{"derivedFrom":makeQuery(id+"F3.boolean.opBoolean","COPY",FACE,{"derivedFrom":makeQuery(id+"F3.opExtrude","SWEPT_FACE",FACE,{"disambiguationData":[OSD([sQuery(id+"F2.wireOp",EDGE,"E18.14.0")])]})}),"instanceName":"1"});
            var Q28;
            Q28=makeQuery(id+"F7.opPattern","COPY",FACE,{"derivedFrom":makeQuery(id+"F3.boolean.opBoolean","COPY",FACE,{"derivedFrom":makeQuery(id+"F3.opExtrude","SWEPT_FACE",FACE,{"disambiguationData":[OSD([sQuery(id+"F2.wireOp",EDGE,"E13.1.8.0")])]})}),"instanceName":"1"});
            var Q29;
            Q29=makeQuery(id+"F7.opPattern","COPY",FACE,{"derivedFrom":makeQuery(id+"F3.boolean.opBoolean","COPY",FACE,{"derivedFrom":makeQuery(id+"F3.opExtrude","SWEPT_FACE",FACE,{"disambiguationData":[OSD([sQuery(id+"F2.wireOp",EDGE,"E17")])]})}),"instanceName":"1"});
            var Q30;
            Q30=sQuery(id+"F0.wireOp",EDGE,"E2");
            circularPattern(context, id + "F8", {"faces" : qUnion([Q0, Q1, Q2, Q3, Q4, Q5, Q6, Q7, Q8, Q9, Q10, Q11, Q12, Q13, Q14, Q15, Q16, Q17, Q18, Q19, Q20, Q21, Q22, Q23, Q24, Q25, Q26, Q27, Q28, Q29]), "axis" : qUnion([Q30]), "angle" : 360 * degree, "instanceCount" : 9, "equalSpace" : true, "patternType" : PatternType.FACE});
        }
        {
            var Q0;
            Q0=makeQuery(id+"F3.boolean.opBoolean","COPY",FACE,{"derivedFrom":makeQuery(id+"F3.opExtrude","SWEPT_FACE",FACE,{"disambiguationData":[OSD([sQuery(id+"F2.wireOp",EDGE,"E18.14.0")])]})});
            var Q1;
            Q1=makeQuery(id+"F3.boolean.opBoolean","COPY",FACE,{"derivedFrom":makeQuery(id+"F3.opExtrude","SWEPT_FACE",FACE,{"disambiguationData":[OSD([sQuery(id+"F2.wireOp",EDGE,"E17")])]})});
            var Q2;
            Q2=makeQuery(id+"F3.boolean.opBoolean","COPY",FACE,{"derivedFrom":makeQuery(id+"F3.opExtrude","SWEPT_FACE",FACE,{"disambiguationData":[OSD([sQuery(id+"F2.wireOp",EDGE,"E18.1.0")])]})});
            var Q3;
            Q3=makeQuery(id+"F3.boolean.opBoolean","COPY",FACE,{"derivedFrom":makeQuery(id+"F3.opExtrude","SWEPT_FACE",FACE,{"disambiguationData":[OSD([sQuery(id+"F2.wireOp",EDGE,"E18.2.0")])]})});
            var Q4;
            Q4=makeQuery(id+"F3.boolean.opBoolean","COPY",FACE,{"derivedFrom":makeQuery(id+"F3.opExtrude","SWEPT_FACE",FACE,{"disambiguationData":[OSD([sQuery(id+"F2.wireOp",EDGE,"E18.3.0")])]})});
            var Q5;
            Q5=makeQuery(id+"F3.boolean.opBoolean","COPY",FACE,{"derivedFrom":makeQuery(id+"F3.opExtrude","SWEPT_FACE",FACE,{"disambiguationData":[OSD([sQuery(id+"F2.wireOp",EDGE,"E18.4.0")])]})});
            var Q6;
            Q6=makeQuery(id+"F3.boolean.opBoolean","COPY",FACE,{"derivedFrom":makeQuery(id+"F3.opExtrude","SWEPT_FACE",FACE,{"disambiguationData":[OSD([sQuery(id+"F2.wireOp",EDGE,"E18.5.0")])]})});
            var Q7;
            Q7=makeQuery(id+"F3.boolean.opBoolean","COPY",FACE,{"derivedFrom":makeQuery(id+"F3.opExtrude","SWEPT_FACE",FACE,{"disambiguationData":[OSD([sQuery(id+"F2.wireOp",EDGE,"E18.6.0")])]})});
            var Q8;
            Q8=makeQuery(id+"F3.boolean.opBoolean","COPY",FACE,{"derivedFrom":makeQuery(id+"F3.opExtrude","SWEPT_FACE",FACE,{"disambiguationData":[OSD([sQuery(id+"F2.wireOp",EDGE,"E18.7.0")])]})});
            var Q9;
            Q9=makeQuery(id+"F3.boolean.opBoolean","COPY",FACE,{"derivedFrom":makeQuery(id+"F3.opExtrude","SWEPT_FACE",FACE,{"disambiguationData":[OSD([sQuery(id+"F2.wireOp",EDGE,"E18.8.0")])]})});
            var Q10;
            Q10=makeQuery(id+"F3.boolean.opBoolean","COPY",FACE,{"derivedFrom":makeQuery(id+"F3.opExtrude","SWEPT_FACE",FACE,{"disambiguationData":[OSD([sQuery(id+"F2.wireOp",EDGE,"E18.9.0")])]})});
            var Q11;
            Q11=makeQuery(id+"F3.boolean.opBoolean","COPY",FACE,{"derivedFrom":makeQuery(id+"F3.opExtrude","SWEPT_FACE",FACE,{"disambiguationData":[OSD([sQuery(id+"F2.wireOp",EDGE,"E18.10.0")])]})});
            var Q12;
            Q12=makeQuery(id+"F3.boolean.opBoolean","COPY",FACE,{"derivedFrom":makeQuery(id+"F3.opExtrude","SWEPT_FACE",FACE,{"disambiguationData":[OSD([sQuery(id+"F2.wireOp",EDGE,"E18.11.0")])]})});
            var Q13;
            Q13=makeQuery(id+"F3.boolean.opBoolean","COPY",FACE,{"derivedFrom":makeQuery(id+"F3.opExtrude","SWEPT_FACE",FACE,{"disambiguationData":[OSD([sQuery(id+"F2.wireOp",EDGE,"E18.12.0")])]})});
            var Q14;
            Q14=makeQuery(id+"F3.boolean.opBoolean","COPY",FACE,{"derivedFrom":makeQuery(id+"F3.opExtrude","SWEPT_FACE",FACE,{"disambiguationData":[OSD([sQuery(id+"F2.wireOp",EDGE,"E18.13.0")])]})});
            var Q15;
            Q15=makeQuery(id+"F3.boolean.opBoolean","COPY",FACE,{"derivedFrom":makeQuery(id+"F3.opExtrude","SWEPT_FACE",FACE,{"disambiguationData":[OSD([sQuery(id+"F2.wireOp",EDGE,"E13.1.8.0")])]})});
            var Q16;
            Q16=makeQuery(id+"F3.boolean.opBoolean","COPY",FACE,{"derivedFrom":makeQuery(id+"F3.opExtrude","SWEPT_FACE",FACE,{"disambiguationData":[OSD([sQuery(id+"F2.wireOp",EDGE,"E11")])]})});
            var Q17;
            Q17=makeQuery(id+"F3.boolean.opBoolean","COPY",FACE,{"derivedFrom":makeQuery(id+"F3.opExtrude","SWEPT_FACE",FACE,{"disambiguationData":[OSD([sQuery(id+"F2.wireOp",EDGE,"E12.1.0")])]})});
            var Q18;
            Q18=makeQuery(id+"F3.boolean.opBoolean","COPY",FACE,{"derivedFrom":makeQuery(id+"F3.opExtrude","SWEPT_FACE",FACE,{"disambiguationData":[OSD([sQuery(id+"F2.wireOp",EDGE,"E6")])]})});
            var Q19;
            Q19=makeQuery(id+"F3.boolean.opBoolean","COPY",FACE,{"derivedFrom":makeQuery(id+"F3.opExtrude","SWEPT_FACE",FACE,{"disambiguationData":[OSD([sQuery(id+"F2.wireOp",EDGE,"E7.4.0")])]})});
            var Q20;
            Q20=makeQuery(id+"F3.boolean.opBoolean","COPY",FACE,{"derivedFrom":makeQuery(id+"F3.opExtrude","SWEPT_FACE",FACE,{"disambiguationData":[OSD([sQuery(id+"F2.wireOp",EDGE,"E13.1.7.0")])]})});
            var Q21;
            Q21=makeQuery(id+"F3.boolean.opBoolean","COPY",FACE,{"derivedFrom":makeQuery(id+"F3.opExtrude","SWEPT_FACE",FACE,{"disambiguationData":[OSD([sQuery(id+"F2.wireOp",EDGE,"E7.3.0")])]})});
            var Q22;
            Q22=makeQuery(id+"F3.boolean.opBoolean","COPY",FACE,{"derivedFrom":makeQuery(id+"F3.opExtrude","SWEPT_FACE",FACE,{"disambiguationData":[OSD([sQuery(id+"F2.wireOp",EDGE,"E5")])]})});
            var Q23;
            Q23=makeQuery(id+"F3.boolean.opBoolean","COPY",FACE,{"derivedFrom":makeQuery(id+"F3.opExtrude","SWEPT_FACE",FACE,{"disambiguationData":[OSD([sQuery(id+"F2.wireOp",EDGE,"E12.2.0")])]})});
            var Q24;
            Q24=makeQuery(id+"F3.boolean.opBoolean","COPY",FACE,{"derivedFrom":makeQuery(id+"F3.opExtrude","SWEPT_FACE",FACE,{"disambiguationData":[OSD([sQuery(id+"F2.wireOp",EDGE,"E7.1.0")])]})});
            var Q25;
            Q25=makeQuery(id+"F3.boolean.opBoolean","COPY",FACE,{"derivedFrom":makeQuery(id+"F3.opExtrude","SWEPT_FACE",FACE,{"disambiguationData":[OSD([sQuery(id+"F2.wireOp",EDGE,"E7.2.0")])]})});
            var Q26;
            Q26=makeQuery(id+"F3.boolean.opBoolean","COPY",FACE,{"derivedFrom":makeQuery(id+"F3.opExtrude","SWEPT_FACE",FACE,{"disambiguationData":[OSD([sQuery(id+"F2.wireOp",EDGE,"E12.5.0")])]})});
            var Q27;
            Q27=makeQuery(id+"F3.boolean.opBoolean","COPY",FACE,{"derivedFrom":makeQuery(id+"F3.opExtrude","SWEPT_FACE",FACE,{"disambiguationData":[OSD([sQuery(id+"F2.wireOp",EDGE,"E12.4.0")])]})});
            var Q28;
            Q28=makeQuery(id+"F3.boolean.opBoolean","COPY",FACE,{"derivedFrom":makeQuery(id+"F3.opExtrude","SWEPT_FACE",FACE,{"disambiguationData":[OSD([sQuery(id+"F2.wireOp",EDGE,"E12.3.0")])]})});
            var Q29;
            Q29=makeQuery(id+"F3.boolean.opBoolean","COPY",FACE,{"derivedFrom":makeQuery(id+"F3.opExtrude","SWEPT_FACE",FACE,{"disambiguationData":[OSD([sQuery(id+"F2.wireOp",EDGE,"E12.6.0")])]})});
            var Q30;
            Q30=sQuery(id+"F4.wireOp",EDGE,"E21");
            circularPattern(context, id + "F9", {"faces" : qUnion([Q0, Q1, Q2, Q3, Q4, Q5, Q6, Q7, Q8, Q9, Q10, Q11, Q12, Q13, Q14, Q15, Q16, Q17, Q18, Q19, Q20, Q21, Q22, Q23, Q24, Q25, Q26, Q27, Q28, Q29]), "axis" : qUnion([Q30]), "angle" : 70 * degree, "instanceCount" : 2, "oppositeDirection" : true, "patternType" : PatternType.FACE});
        }
        {
            var Q0;
            Q0=makeQuery(id+"F9.opPattern","COPY",FACE,{"derivedFrom":makeQuery(id+"F3.boolean.opBoolean","COPY",FACE,{"derivedFrom":makeQuery(id+"F3.opExtrude","SWEPT_FACE",FACE,{"disambiguationData":[OSD([sQuery(id+"F2.wireOp",EDGE,"E18.13.0")])]})}),"instanceName":"1"});
            var Q1;
            Q1=makeQuery(id+"F9.opPattern","COPY",FACE,{"derivedFrom":makeQuery(id+"F3.boolean.opBoolean","COPY",FACE,{"derivedFrom":makeQuery(id+"F3.opExtrude","SWEPT_FACE",FACE,{"disambiguationData":[OSD([sQuery(id+"F2.wireOp",EDGE,"E18.12.0")])]})}),"instanceName":"1"});
            var Q2;
            Q2=makeQuery(id+"F9.opPattern","COPY",FACE,{"derivedFrom":makeQuery(id+"F3.boolean.opBoolean","COPY",FACE,{"derivedFrom":makeQuery(id+"F3.opExtrude","SWEPT_FACE",FACE,{"disambiguationData":[OSD([sQuery(id+"F2.wireOp",EDGE,"E18.11.0")])]})}),"instanceName":"1"});
            var Q3;
            Q3=makeQuery(id+"F9.opPattern","COPY",FACE,{"derivedFrom":makeQuery(id+"F3.boolean.opBoolean","COPY",FACE,{"derivedFrom":makeQuery(id+"F3.opExtrude","SWEPT_FACE",FACE,{"disambiguationData":[OSD([sQuery(id+"F2.wireOp",EDGE,"E18.10.0")])]})}),"instanceName":"1"});
            var Q4;
            Q4=makeQuery(id+"F9.opPattern","COPY",FACE,{"derivedFrom":makeQuery(id+"F3.boolean.opBoolean","COPY",FACE,{"derivedFrom":makeQuery(id+"F3.opExtrude","SWEPT_FACE",FACE,{"disambiguationData":[OSD([sQuery(id+"F2.wireOp",EDGE,"E18.9.0")])]})}),"instanceName":"1"});
            var Q5;
            Q5=makeQuery(id+"F9.opPattern","COPY",FACE,{"derivedFrom":makeQuery(id+"F3.boolean.opBoolean","COPY",FACE,{"derivedFrom":makeQuery(id+"F3.opExtrude","SWEPT_FACE",FACE,{"disambiguationData":[OSD([sQuery(id+"F2.wireOp",EDGE,"E18.8.0")])]})}),"instanceName":"1"});
            var Q6;
            Q6=makeQuery(id+"F9.opPattern","COPY",FACE,{"derivedFrom":makeQuery(id+"F3.boolean.opBoolean","COPY",FACE,{"derivedFrom":makeQuery(id+"F3.opExtrude","SWEPT_FACE",FACE,{"disambiguationData":[OSD([sQuery(id+"F2.wireOp",EDGE,"E18.7.0")])]})}),"instanceName":"1"});
            var Q7;
            Q7=makeQuery(id+"F9.opPattern","COPY",FACE,{"derivedFrom":makeQuery(id+"F3.boolean.opBoolean","COPY",FACE,{"derivedFrom":makeQuery(id+"F3.opExtrude","SWEPT_FACE",FACE,{"disambiguationData":[OSD([sQuery(id+"F2.wireOp",EDGE,"E18.6.0")])]})}),"instanceName":"1"});
            var Q8;
            Q8=makeQuery(id+"F9.opPattern","COPY",FACE,{"derivedFrom":makeQuery(id+"F3.boolean.opBoolean","COPY",FACE,{"derivedFrom":makeQuery(id+"F3.opExtrude","SWEPT_FACE",FACE,{"disambiguationData":[OSD([sQuery(id+"F2.wireOp",EDGE,"E18.5.0")])]})}),"instanceName":"1"});
            var Q9;
            Q9=makeQuery(id+"F9.opPattern","COPY",FACE,{"derivedFrom":makeQuery(id+"F3.boolean.opBoolean","COPY",FACE,{"derivedFrom":makeQuery(id+"F3.opExtrude","SWEPT_FACE",FACE,{"disambiguationData":[OSD([sQuery(id+"F2.wireOp",EDGE,"E18.4.0")])]})}),"instanceName":"1"});
            var Q10;
            Q10=makeQuery(id+"F9.opPattern","COPY",FACE,{"derivedFrom":makeQuery(id+"F3.boolean.opBoolean","COPY",FACE,{"derivedFrom":makeQuery(id+"F3.opExtrude","SWEPT_FACE",FACE,{"disambiguationData":[OSD([sQuery(id+"F2.wireOp",EDGE,"E18.3.0")])]})}),"instanceName":"1"});
            var Q11;
            Q11=makeQuery(id+"F9.opPattern","COPY",FACE,{"derivedFrom":makeQuery(id+"F3.boolean.opBoolean","COPY",FACE,{"derivedFrom":makeQuery(id+"F3.opExtrude","SWEPT_FACE",FACE,{"disambiguationData":[OSD([sQuery(id+"F2.wireOp",EDGE,"E18.2.0")])]})}),"instanceName":"1"});
            var Q12;
            Q12=makeQuery(id+"F9.opPattern","COPY",FACE,{"derivedFrom":makeQuery(id+"F3.boolean.opBoolean","COPY",FACE,{"derivedFrom":makeQuery(id+"F3.opExtrude","SWEPT_FACE",FACE,{"disambiguationData":[OSD([sQuery(id+"F2.wireOp",EDGE,"E18.1.0")])]})}),"instanceName":"1"});
            var Q13;
            Q13=makeQuery(id+"F9.opPattern","COPY",FACE,{"derivedFrom":makeQuery(id+"F3.boolean.opBoolean","COPY",FACE,{"derivedFrom":makeQuery(id+"F3.opExtrude","SWEPT_FACE",FACE,{"disambiguationData":[OSD([sQuery(id+"F2.wireOp",EDGE,"E17")])]})}),"instanceName":"1"});
            var Q14;
            Q14=makeQuery(id+"F9.opPattern","COPY",FACE,{"derivedFrom":makeQuery(id+"F3.boolean.opBoolean","COPY",FACE,{"derivedFrom":makeQuery(id+"F3.opExtrude","SWEPT_FACE",FACE,{"disambiguationData":[OSD([sQuery(id+"F2.wireOp",EDGE,"E18.14.0")])]})}),"instanceName":"1"});
            var Q15;
            Q15=makeQuery(id+"F9.opPattern","COPY",FACE,{"derivedFrom":makeQuery(id+"F3.boolean.opBoolean","COPY",FACE,{"derivedFrom":makeQuery(id+"F3.opExtrude","SWEPT_FACE",FACE,{"disambiguationData":[OSD([sQuery(id+"F2.wireOp",EDGE,"E11")])]})}),"instanceName":"1"});
            var Q16;
            Q16=makeQuery(id+"F9.opPattern","COPY",FACE,{"derivedFrom":makeQuery(id+"F3.boolean.opBoolean","COPY",FACE,{"derivedFrom":makeQuery(id+"F3.opExtrude","SWEPT_FACE",FACE,{"disambiguationData":[OSD([sQuery(id+"F2.wireOp",EDGE,"E13.1.8.0")])]})}),"instanceName":"1"});
            var Q17;
            Q17=makeQuery(id+"F9.opPattern","COPY",FACE,{"derivedFrom":makeQuery(id+"F3.boolean.opBoolean","COPY",FACE,{"derivedFrom":makeQuery(id+"F3.opExtrude","SWEPT_FACE",FACE,{"disambiguationData":[OSD([sQuery(id+"F2.wireOp",EDGE,"E13.1.7.0")])]})}),"instanceName":"1"});
            var Q18;
            Q18=makeQuery(id+"F9.opPattern","COPY",FACE,{"derivedFrom":makeQuery(id+"F3.boolean.opBoolean","COPY",FACE,{"derivedFrom":makeQuery(id+"F3.opExtrude","SWEPT_FACE",FACE,{"disambiguationData":[OSD([sQuery(id+"F2.wireOp",EDGE,"E12.6.0")])]})}),"instanceName":"1"});
            var Q19;
            Q19=makeQuery(id+"F9.opPattern","COPY",FACE,{"derivedFrom":makeQuery(id+"F3.boolean.opBoolean","COPY",FACE,{"derivedFrom":makeQuery(id+"F3.opExtrude","SWEPT_FACE",FACE,{"disambiguationData":[OSD([sQuery(id+"F2.wireOp",EDGE,"E12.5.0")])]})}),"instanceName":"1"});
            var Q20;
            Q20=makeQuery(id+"F9.opPattern","COPY",FACE,{"derivedFrom":makeQuery(id+"F3.boolean.opBoolean","COPY",FACE,{"derivedFrom":makeQuery(id+"F3.opExtrude","SWEPT_FACE",FACE,{"disambiguationData":[OSD([sQuery(id+"F2.wireOp",EDGE,"E12.4.0")])]})}),"instanceName":"1"});
            var Q21;
            Q21=makeQuery(id+"F9.opPattern","COPY",FACE,{"derivedFrom":makeQuery(id+"F3.boolean.opBoolean","COPY",FACE,{"derivedFrom":makeQuery(id+"F3.opExtrude","SWEPT_FACE",FACE,{"disambiguationData":[OSD([sQuery(id+"F2.wireOp",EDGE,"E12.3.0")])]})}),"instanceName":"1"});
            var Q22;
            Q22=makeQuery(id+"F9.opPattern","COPY",FACE,{"derivedFrom":makeQuery(id+"F3.boolean.opBoolean","COPY",FACE,{"derivedFrom":makeQuery(id+"F3.opExtrude","SWEPT_FACE",FACE,{"disambiguationData":[OSD([sQuery(id+"F2.wireOp",EDGE,"E12.2.0")])]})}),"instanceName":"1"});
            var Q23;
            Q23=makeQuery(id+"F9.opPattern","COPY",FACE,{"derivedFrom":makeQuery(id+"F3.boolean.opBoolean","COPY",FACE,{"derivedFrom":makeQuery(id+"F3.opExtrude","SWEPT_FACE",FACE,{"disambiguationData":[OSD([sQuery(id+"F2.wireOp",EDGE,"E12.1.0")])]})}),"instanceName":"1"});
            var Q24;
            Q24=makeQuery(id+"F9.opPattern","COPY",FACE,{"derivedFrom":makeQuery(id+"F3.boolean.opBoolean","COPY",FACE,{"derivedFrom":makeQuery(id+"F3.opExtrude","SWEPT_FACE",FACE,{"disambiguationData":[OSD([sQuery(id+"F2.wireOp",EDGE,"E6")])]})}),"instanceName":"1"});
            var Q25;
            Q25=makeQuery(id+"F9.opPattern","COPY",FACE,{"derivedFrom":makeQuery(id+"F3.boolean.opBoolean","COPY",FACE,{"derivedFrom":makeQuery(id+"F3.opExtrude","SWEPT_FACE",FACE,{"disambiguationData":[OSD([sQuery(id+"F2.wireOp",EDGE,"E7.4.0")])]})}),"instanceName":"1"});
            var Q26;
            Q26=makeQuery(id+"F9.opPattern","COPY",FACE,{"derivedFrom":makeQuery(id+"F3.boolean.opBoolean","COPY",FACE,{"derivedFrom":makeQuery(id+"F3.opExtrude","SWEPT_FACE",FACE,{"disambiguationData":[OSD([sQuery(id+"F2.wireOp",EDGE,"E7.3.0")])]})}),"instanceName":"1"});
            var Q27;
            Q27=makeQuery(id+"F9.opPattern","COPY",FACE,{"derivedFrom":makeQuery(id+"F3.boolean.opBoolean","COPY",FACE,{"derivedFrom":makeQuery(id+"F3.opExtrude","SWEPT_FACE",FACE,{"disambiguationData":[OSD([sQuery(id+"F2.wireOp",EDGE,"E7.2.0")])]})}),"instanceName":"1"});
            var Q28;
            Q28=makeQuery(id+"F9.opPattern","COPY",FACE,{"derivedFrom":makeQuery(id+"F3.boolean.opBoolean","COPY",FACE,{"derivedFrom":makeQuery(id+"F3.opExtrude","SWEPT_FACE",FACE,{"disambiguationData":[OSD([sQuery(id+"F2.wireOp",EDGE,"E7.1.0")])]})}),"instanceName":"1"});
            var Q29;
            Q29=makeQuery(id+"F9.opPattern","COPY",FACE,{"derivedFrom":makeQuery(id+"F3.boolean.opBoolean","COPY",FACE,{"derivedFrom":makeQuery(id+"F3.opExtrude","SWEPT_FACE",FACE,{"disambiguationData":[OSD([sQuery(id+"F2.wireOp",EDGE,"E5")])]})}),"instanceName":"1"});
            var Q30;
            Q30=sQuery(id+"F0.wireOp",EDGE,"E2");
            circularPattern(context, id + "F10", {"faces" : qUnion([Q0, Q1, Q2, Q3, Q4, Q5, Q6, Q7, Q8, Q9, Q10, Q11, Q12, Q13, Q14, Q15, Q16, Q17, Q18, Q19, Q20, Q21, Q22, Q23, Q24, Q25, Q26, Q27, Q28, Q29]), "axis" : qUnion([Q30]), "angle" : 360 * degree, "instanceCount" : 13, "equalSpace" : true, "patternType" : PatternType.FACE});
        }
    });
